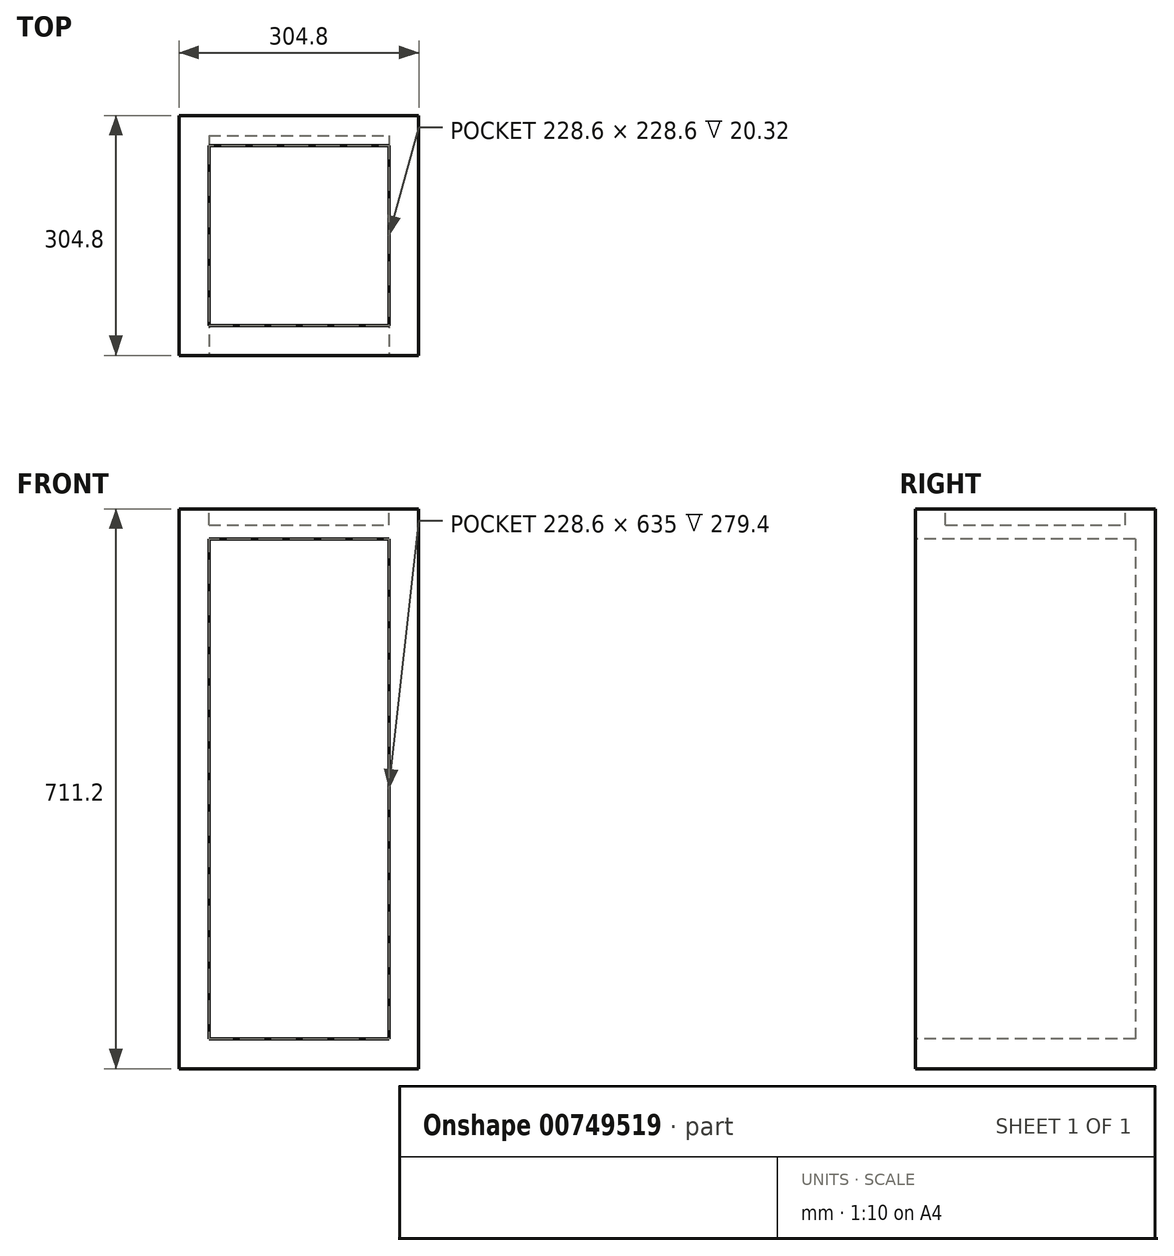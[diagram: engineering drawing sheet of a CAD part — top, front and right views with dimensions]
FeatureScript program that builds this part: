
annotation { "Feature Type Name" : "Feature", "Feature Type Description" : "" }
export const myFeature = defineFeature(function(context is Context, id is Id, definition is map)
    precondition{}
    {
        {
            var Q0;
            Q0=qCreatedBy(makeId("Top.planeOp"),FACE);
            var sketch = newSketch(context, id + "F0", { "sketchPlane" : qUnion([Q0])});
            skLineSegment(sketch, "E0.bottom", {"start": v(-112.33, -182.5) * mm, "end": v(192.47, -182.5) * mm});
            skLineSegment(sketch, "E0.top", {"start": v(-112.33, 122.3) * mm, "end": v(192.47, 122.3) * mm});
            skLineSegment(sketch, "E0.left", {"start": v(-112.33, -182.5) * mm, "end": v(-112.33, 122.3) * mm});
            skLineSegment(sketch, "E0.right", {"start": v(192.47, -182.5) * mm, "end": v(192.47, 122.3) * mm});
            skSolve(sketch);
        }
        {
            var Q0;
            Q0=makeQuery(id+"F0.imprint","IMPRINT",FACE,{"disambiguationData":[TD([[makeQuery(id+"F0.imprint","IMPRINT",EDGE,{"derivedFrom":sQuery(id+"F0.wireOp",EDGE,"E0.bottom")}),1.0]])]});
            extrude(context, id + "F1", {"entities" : qUnion([Q0]), "depth" : 711.2 * mm, "offsetDistance" : 25.4 * mm});
        }
        {
            var Q0;
            Q0=makeQuery(id+"F1.opExtrude","SWEPT_FACE",FACE,{"disambiguationData":[OSD([sQuery(id+"F0.wireOp",EDGE,"E0.bottom")])]});
            var sketch = newSketch(context, id + "F2", { "sketchPlane" : qUnion([Q0])});
            skLineSegment(sketch, "E1.0", {"start": v(-74.23, 673.1) * mm, "end": v(-74.23, 38.1) * mm});
            skLineSegment(sketch, "E2.0", {"start": v(-74.23, 673.1) * mm, "end": v(154.37, 673.1) * mm});
            skLineSegment(sketch, "E3.0", {"start": v(154.37, 673.1) * mm, "end": v(154.37, 38.1) * mm});
            skLineSegment(sketch, "E4.0", {"start": v(-74.23, 38.1) * mm, "end": v(154.37, 38.1) * mm});
            skSolve(sketch);
        }
        {
            var Q0;
            Q0=makeQuery(id+"F2.imprint","IMPRINT",FACE,{"disambiguationData":[TD([[makeQuery(id+"F2.imprint","IMPRINT",EDGE,{"derivedFrom":sQuery(id+"F2.wireOp",EDGE,"E1.0")}),1.0]])]});
            extrude(context, id + "F3", {"entities" : qUnion([Q0]), "operationType" : NewBodyOperationType.REMOVE, "oppositeDirection" : true, "depth" : 279.4 * mm, "offsetDistance" : 25.4 * mm});
        }
        {
            var Q0;
            Q0=makeQuery(id+"F1.opExtrude","CAP_FACE",FACE,{"disambiguationData":[OSD([sQuery(id+"F0.wireOp",EDGE,"E0.bottom"),sQuery(id+"F0.wireOp",EDGE,"E0.top"),sQuery(id+"F0.wireOp",EDGE,"E0.left"),sQuery(id+"F0.wireOp",EDGE,"E0.right")])],"isStart":false});
            var sketch = newSketch(context, id + "F4", { "sketchPlane" : qUnion([Q0])});
            skLineSegment(sketch, "E5.0", {"start": v(-74.23, -144.4) * mm, "end": v(-74.23, 84.2) * mm});
            skLineSegment(sketch, "E6.0", {"start": v(-74.23, 84.2) * mm, "end": v(154.37, 84.2) * mm});
            skLineSegment(sketch, "E7.0", {"start": v(154.37, -144.4) * mm, "end": v(154.37, 84.2) * mm});
            skLineSegment(sketch, "E8.trimOffspring", {"start": v(-74.23, 115.96) * mm, "end": v(-74.23, 122.3) * mm});
            skLineSegment(sketch, "E9.0", {"start": v(-74.23, -144.4) * mm, "end": v(154.37, -144.4) * mm});
            skLineSegment(sketch, "E10.trimOffspring", {"start": v(186.12, -144.4) * mm, "end": v(192.47, -144.4) * mm});
            skLineSegment(sketch, "E11.trimOffspring", {"start": v(154.37, 115.96) * mm, "end": v(154.37, 122.3) * mm});
            skSolve(sketch);
        }
        {
            var Q0;
            Q0=makeQuery(id+"F4.imprint","IMPRINT",FACE,{"disambiguationData":[TD([[makeQuery(id+"F4.imprint","IMPRINT",EDGE,{"derivedFrom":sQuery(id+"F4.wireOp",EDGE,"E5.0")}),-1.0]])]});
            extrude(context, id + "F5", {"entities" : qUnion([Q0]), "operationType" : NewBodyOperationType.REMOVE, "oppositeDirection" : true, "depth" : 20.32 * mm, "offsetDistance" : 25.4 * mm});
        }
    });
